# Revit family: SC_TubestOne
name_source: partatom
category: Structural Columns
units: mm (PartAtom-declared; Revit-internal decimal feet)

## family parameters
Always export as geometry = No
Beam cutback in plan = From bounding box
Cut with Voids When Loaded = No
Material for Model Behavior = Steel
Section Shape = Not Defined
Shared = No
Show family pre-cut in plan views = Yes

## types (10) — shared parameters
D = 20 mm
R = 10 mm
h2 = 25 mm

## per-type parameters (varying)
| type | B | H | e |
| TUBEST O 500x200x5 | 200 mm | 500 mm | 5 mm |
| TUBEST O 300x150x4 | 150 mm | 300 mm | 4 mm |
| TUBEST O 300x200x4 | 200 mm | 300 mm | 4 mm |
| TUBEST O 350x150x4 | 150 mm | 350 mm | 4 mm |
| TUBEST O 350x200x4 | 200 mm | 350 mm | 4 mm |
| TUBEST O 400x150x4 | 150 mm | 400 mm | 4 mm |
| TUBEST O 400x200x4 | 200 mm | 400 mm | 4 mm |
| TUBEST O 450x150x4 | 150 mm | 450 mm | 4 mm |
| TUBEST O 450x200x4 | 200 mm | 450 mm | 4 mm |
| TUBEST O 500x200x4 | 200 mm | 500 mm | 4 mm |

## geometry (parser evidence)
native form markers: Blend x4, Sweep x1
no freeform markers — native parametric forms only
